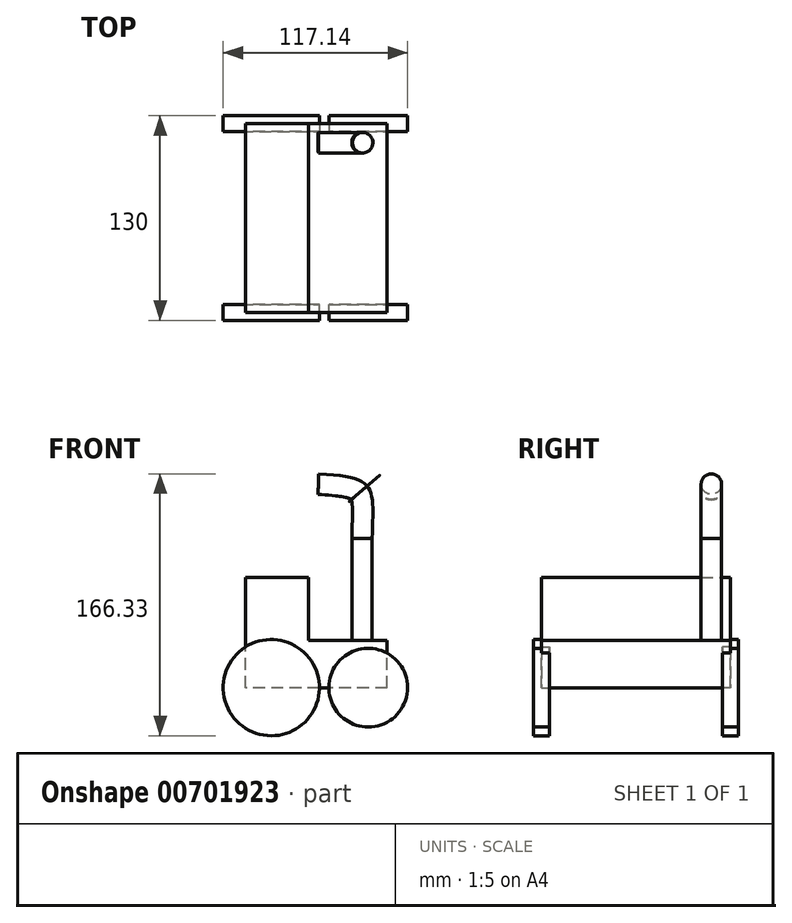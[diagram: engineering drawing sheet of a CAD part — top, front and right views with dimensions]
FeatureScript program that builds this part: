
annotation { "Feature Type Name" : "Feature", "Feature Type Description" : "" }
export const myFeature = defineFeature(function(context is Context, id is Id, definition is map)
    precondition{}
    {
        {
            var Q0;
            Q0=qCreatedBy(makeId("Front.planeOp"),FACE);
            var sketch = newSketch(context, id + "F0", { "sketchPlane" : qUnion([Q0])});
            skLineSegment(sketch, "E0.bottom", {"start": v(45, -15) * mm, "end": v(-45, -15) * mm});
            skLineSegment(sketch, "E0.top", {"start": v(45, 15) * mm, "end": v(-45, 15) * mm});
            skLineSegment(sketch, "E0.left", {"start": v(45, -15) * mm, "end": v(45, 15) * mm});
            skLineSegment(sketch, "E0.right", {"start": v(-45, -15) * mm, "end": v(-45, 15) * mm});
            skPoint(sketch, "E0.middle", {"position": v(0, 0) * mm});
            skLineSegment(sketch, "E1.bottom", {"start": v(-45, 15) * mm, "end": v(-5, 15) * mm});
            skLineSegment(sketch, "E1.top", {"start": v(-45, 55) * mm, "end": v(-5, 55) * mm});
            skLineSegment(sketch, "E1.left", {"start": v(-45, 15) * mm, "end": v(-45, 55) * mm});
            skLineSegment(sketch, "E1.right", {"start": v(-5, 15) * mm, "end": v(-5, 55) * mm});
            skSolve(sketch);
        }
        {
            var Q0;
            Q0 = qSketchRegion(id + "F0", true);
            extrude(context, id + "F1", {"entities" : qUnion([Q0]), "depth" : 60 * mm, "offsetDistance" : 25 * mm});
        }
        {
            var Q0;
            Q0=qCreatedBy(makeId("Front.planeOp"),FACE);
            cPlane(context, id + "F2", {"entities" : qUnion([Q0]), "cplaneType" : CPlaneType.OFFSET, "offset" : 60 * mm, "width" : 150 * mm, "height" : 150 * mm});
        }
        {
            var Q0;
            Q0=qCreatedBy(id+"F2.planeOp",FACE);
            var sketch = newSketch(context, id + "F3", { "sketchPlane" : qUnion([Q0])});
            skCircle(sketch, "E2", {"center": v(-28.59, -14.91) * mm, "radius": 30.55 * mm});
            skSolve(sketch);
        }
        {
            var Q0;
            Q0=makeQuery(id+"F3.imprint","IMPRINT",FACE,{"disambiguationData":[TD([[makeQuery(id+"F3.imprint","IMPRINT",EDGE,{"derivedFrom":sQuery(id+"F3.wireOp",EDGE,"E2")}),1.0]])]});
            extrude(context, id + "F4", {"entities" : qUnion([Q0]), "operationType" : NewBodyOperationType.ADD, "endBound" : BoundingType.SYMMETRIC, "depth" : 10 * mm, "offsetDistance" : 25 * mm});
        }
        {
            var Q0;
            Q0=qCreatedBy(id+"F2.planeOp",FACE);
            var sketch = newSketch(context, id + "F5", { "sketchPlane" : qUnion([Q0])});
            skCircle(sketch, "E3", {"center": v(33, -14.91) * mm, "radius": 25 * mm});
            skSolve(sketch);
        }
        {
            var Q0;
            Q0 = qSketchRegion(id + "F5", true);
            extrude(context, id + "F6", {"entities" : qUnion([Q0]), "operationType" : NewBodyOperationType.ADD, "endBound" : BoundingType.SYMMETRIC, "depth" : 10 * mm, "offsetDistance" : 25 * mm});
        }
        {
            var Q0;
            Q0=makeQuery(id+"F1.opExtrude","SWEPT_BODY",BODY,{"disambiguationData":[OSD([sQuery(id+"F0.wireOp",EDGE,"E0.bottom"),sQuery(id+"F0.wireOp",EDGE,"E0.top"),sQuery(id+"F0.wireOp",EDGE,"E0.left"),sQuery(id+"F0.wireOp",EDGE,"E0.right"),sQuery(id+"F0.wireOp",EDGE,"E1.top"),sQuery(id+"F0.wireOp",EDGE,"E1.left"),sQuery(id+"F0.wireOp",EDGE,"E1.right")])]});
            var Q1;
            Q1=qCreatedBy(makeId("Front.planeOp"),FACE);
            mirror(context, id + "F7", {"operationType" : NewBodyOperationType.ADD, "entities" : qUnion([Q0]), "mirrorPlane" : qUnion([Q1])});
        }
        {
            var Q0;
            Q0=qCreatedBy(makeId("Top.planeOp"),FACE);
            var sketch = newSketch(context, id + "F8", { "sketchPlane" : qUnion([Q0])});
            skCircle(sketch, "E4", {"center": v(29.04, 47.9) * mm, "radius": 6.5 * mm});
            skSolve(sketch);
        }
        {
            var Q0;
            Q0 = qSketchRegion(id + "F8", true);
            extrude(context, id + "F9", {"entities" : qUnion([Q0]), "operationType" : NewBodyOperationType.ADD, "depth" : 80 * mm, "offsetDistance" : 25 * mm});
        }
        {
            var Q0;
            Q0=makeQuery(id+"F9.opExtrude","CAP_FACE",FACE,{"disambiguationData":[OSD([sQuery(id+"F8.wireOp",EDGE,"E4")])],"isStart":false});
            var sketch = newSketch(context, id + "F10", { "sketchPlane" : qUnion([Q0])});
            skPoint(sketch, "E5", {"position": v(35.54, 47.79) * mm});
            skSolve(sketch);
        }
        {
            var Q0;
            Q0=qCreatedBy(makeId("Front.planeOp"),FACE);
            var Q1;
            Q1=sQuery(id+"F10.wireOp",VERTEX,"E5");
            cPlane(context, id + "F11", {"entities" : qUnion([Q0, Q1]), "cplaneType" : CPlaneType.PLANE_POINT, "offset" : 59 * mm, "oppositeDirection" : true, "width" : 150 * mm, "height" : 150 * mm});
        }
        {
            var Q0;
            Q0=qCreatedBy(id+"F11.planeOp",FACE);
            var sketch = newSketch(context, id + "F12", { "sketchPlane" : qUnion([Q0])});
            skFitSpline(sketch, "E6", {"points": [v(35, 79.82) * mm, v(33.27, 110.51) * mm, v(1.54, 120.32) * mm], "startDerivative": vector(1.78, 88.73) * mm, "endDerivative": vector(-122.1, 6.78) * mm});
            skSolve(sketch);
        }
        {
            var Q0;
            Q0=makeQuery(id+"F10.imprint","IMPRINT",FACE,{"disambiguationData":[TD([[makeQuery(id+"F10.imprint","IMPRINT",EDGE,{"derivedFrom":makeQuery(id+"F9.opExtrude","CAP_EDGE",EDGE,{"disambiguationData":[OSD([sQuery(id+"F8.wireOp",EDGE,"E4")])],"isStart":false})}),1.0]])]});
            var Q1;
            Q1=sQuery(id+"F12.wireOp",EDGE,"E6");
            sweep(context, id + "F13", {"operationType" : NewBodyOperationType.ADD, "profiles" : qUnion([Q0]), "path" : qUnion([Q1])});
        }
    });
